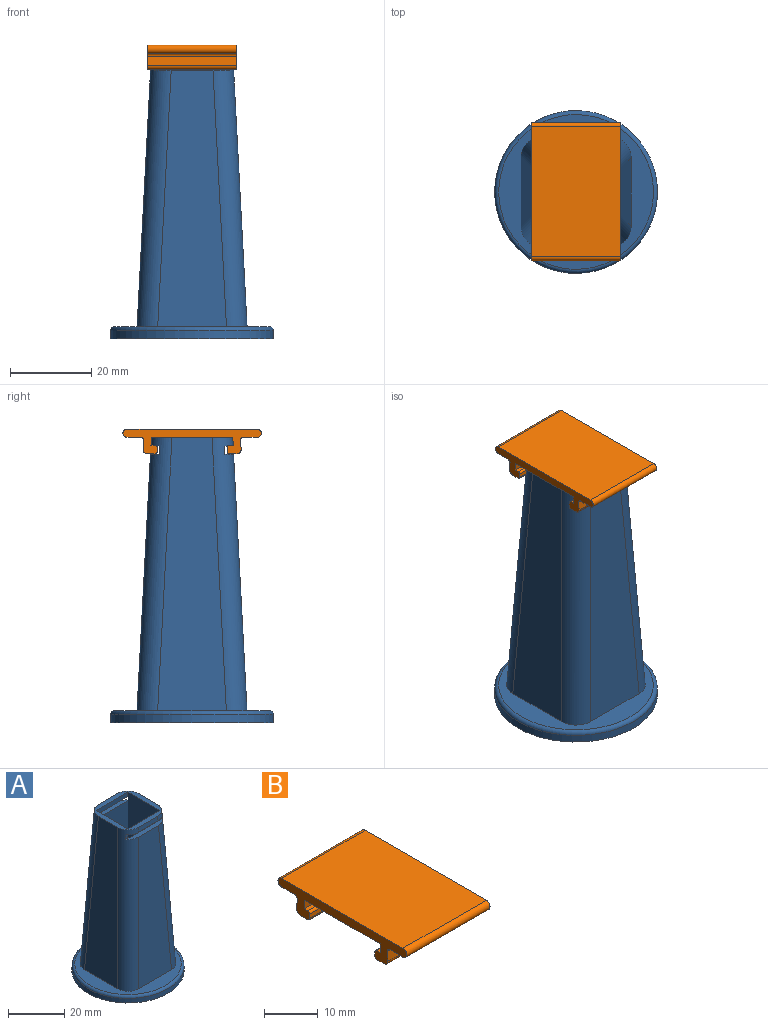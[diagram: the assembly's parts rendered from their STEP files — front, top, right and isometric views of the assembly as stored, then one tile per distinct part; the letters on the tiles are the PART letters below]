
ASSEMBLY  parts=2 mates=1
PART A: 28 faces, bbox 43.3x43.3x70.1 mm
  f0: plane 67x16.88mm, normal (1,0,0.05), area 896.7mm2, adj f8,f11,f13,f23
  f1: plane 63x16.88mm, normal (0,1,0.05), area 856.4mm2, adj f8,f9,f22,f23
  f2: plane 67x16.88mm, normal (-1,0,0.05), area 896.7mm2, adj f9,f10,f13,f23
  f3: plane 63x16.88mm, normal (0,-1,0.05), area 856.4mm2, adj f10,f11,f18,f23
  f4: plane 67x23.02mm, normal (-1,0,-0.05), area 1308.5mm2, adj f5,f7,f12,f13,f16,f18,f19,f21
  f5: plane 63x23.02mm, normal (0,-1,-0.05), area 1243.8mm2, adj f4,f6,f22,f25
  f6: plane 67x23.02mm, normal (1,0,-0.05), area 1308.5mm2, adj f5,f7,f12,f13,f16,f18,f19,f21
  f7: plane 63x23.02mm, normal (0,1,-0.05), area 1243.8mm2, adj f4,f6,f18,f25
  f8: cylinder r=5.08mm len=67.22mm, axis (-0.05,-0.05,1), area 525.7mm2, adj f0,f1,f13,f14,f20,f21,f22,f23
  f9: cylinder r=5.08mm len=67.22mm, axis (0.05,-0.05,1), area 525.7mm2, adj f1,f2,f13,f14,f20,f21,f22,f23
  f10: cylinder r=5.08mm len=67.22mm, axis (0.05,0.05,1), area 525.7mm2, adj f2,f3,f13,f15,f17,f18,f19,f23
  f11: cylinder r=5.08mm len=67.22mm, axis (-0.05,0.05,1), area 525.7mm2, adj f0,f3,f13,f15,f17,f18,f19,f23
  f12: plane 16.21x2.05mm, normal (0,-1,-0.05), area 33.1mm2, adj f4,f6,f13,f21
  f13: plane 20x20mm, normal (0,0,1), area 122.1mm2, adj f0,f2,f4,f6,f8,f9,f10,f11
  f14: plane 10.06x2mm, normal (0,1,0.05), area 19.9mm2, adj f8,f9,f13,f20
  f15: plane 10.06x2mm, normal (0,-1,0.05), area 19.9mm2, adj f10,f11,f13,f17
  f16: plane 16.21x2.05mm, normal (0,1,-0.05), area 33.1mm2, adj f4,f6,f13,f19
  f17: plane 18.14x2mm, normal (0,0,-1), area 31.4mm2, adj f10,f11,f15,f19
  f18: plane 18.5x2.11mm, normal (0,0,1), area 32.1mm2, adj f3,f4,f6,f7,f10,f11,f19
  f19: plane 18.51x2.01mm, normal (0,-1,0), area 4.9mm2, adj f4,f6,f10,f11,f16,f17,f18
  f20: plane 18.14x2mm, normal (0,0,-1), area 31.4mm2, adj f8,f9,f14,f21
  f21: plane 18.51x2.01mm, normal (0,1,0), area 4.9mm2, adj f4,f6,f8,f9,f12,f20,f22
  f22: plane 18.5x2.11mm, normal (0,0,1), area 32.1mm2, adj f1,f4,f5,f6,f8,f9,f21
  f23: plane 38x38mm, normal (0,0,1), area 426mm2, adj f0,f1,f2,f3,f8,f9,f10,f11
  f24: cylinder r=20mm len=40mm, axis (0,0,-1), area 251.3mm2, adj f26,f27
  f25: plane 23.02x23.02mm, normal (0,0,1), area 529.8mm2, adj f4,f5,f6,f7
  f26: plane 40x40mm, normal (0,0,-1), area 1256.6mm2, adj f24
  f27: torus R=19mm, axis (0,0,-1), area 193.8mm2, adj f23,f24
PART B: 26 faces, bbox 22x34x6 mm
  f0: plane 32x22mm, normal (0,0,1), area 704mm2, adj f1,f23,f24,f25
  f1: cylinder r=1mm len=22mm, axis (-1,0,0), area 69.1mm2, adj f0,f2,f24,f25
  f2: plane 22x3.37mm, normal (0,0,-1), area 74.1mm2, adj f1,f3,f24,f25
  f3: cylinder r=0.7mm len=22mm, axis (-1,0,0), area 25mm2, adj f2,f4,f24,f25
  f4: plane 22x2.21mm, normal (0,-1,0.05), area 48.7mm2, adj f3,f5,f24,f25
  f5: cylinder r=1mm len=22mm, axis (-1,0,0), area 35.7mm2, adj f4,f6,f24,f25
  f6: plane 22x1.95mm, normal (0,0,-1), area 42.8mm2, adj f5,f7,f24,f25
  f7: cylinder r=0.5mm len=22mm, axis (-1,0,0), area 17.3mm2, adj f6,f8,f24,f25
  f8: plane 22x1mm, normal (0,1,0), area 22mm2, adj f7,f9,f24,f25
  f9: cylinder r=0.5mm len=22mm, axis (-1,0,0), area 17.3mm2, adj f8,f10,f24,f25
  f10: plane 22x1mm, normal (0,0,1), area 22mm2, adj f9,f11,f24,f25
  f11: plane 22x2mm, normal (0,1,-0.05), area 44.1mm2, adj f10,f12,f24,f25
  f12: plane 22x20mm, normal (0,0,-1), area 440mm2, adj f11,f13,f24,f25
  f13: plane 22x2mm, normal (0,-1,-0.05), area 44.1mm2, adj f12,f14,f24,f25
  f14: plane 22x1mm, normal (0,0,1), area 22mm2, adj f13,f15,f24,f25
  f15: cylinder r=0.5mm len=22mm, axis (-1,0,0), area 17.3mm2, adj f14,f16,f24,f25
  f16: plane 22x1mm, normal (0,-1,0), area 22mm2, adj f15,f17,f24,f25
  f17: cylinder r=0.5mm len=22mm, axis (-1,0,0), area 17.3mm2, adj f16,f18,f24,f25
  f18: plane 22x1.95mm, normal (0,0,-1), area 42.8mm2, adj f17,f19,f24,f25
  f19: cylinder r=1mm len=22mm, axis (-1,0,0), area 35.7mm2, adj f18,f20,f24,f25
  f20: plane 22x2.21mm, normal (0,1,0.05), area 48.7mm2, adj f19,f21,f24,f25
  f21: cylinder r=0.7mm len=22mm, axis (-1,0,0), area 25mm2, adj f20,f22,f24,f25
  f22: plane 22x3.37mm, normal (0,0,-1), area 74.1mm2, adj f21,f23,f24,f25
  f23: cylinder r=1mm len=22mm, axis (-1,0,0), area 69.1mm2, adj f0,f22,f24,f25
  f24: plane 34x6mm, normal (1,0,0), area 88.1mm2, adj f0,f1,f2,f3,f4,f5,f6,f7
  f25: plane 34x6mm, normal (-1,0,0), area 88.1mm2, adj f0,f1,f2,f3,f4,f5,f6,f7
PLACE A t=(-10.44,5.04,31.38)mm
PLACE B t=(-10.44,5.01,31.54)mm
MATE slider B.f8 <-> A.f19  axis (0,1,0) through (-10.44,-3.59,28.54)mm
